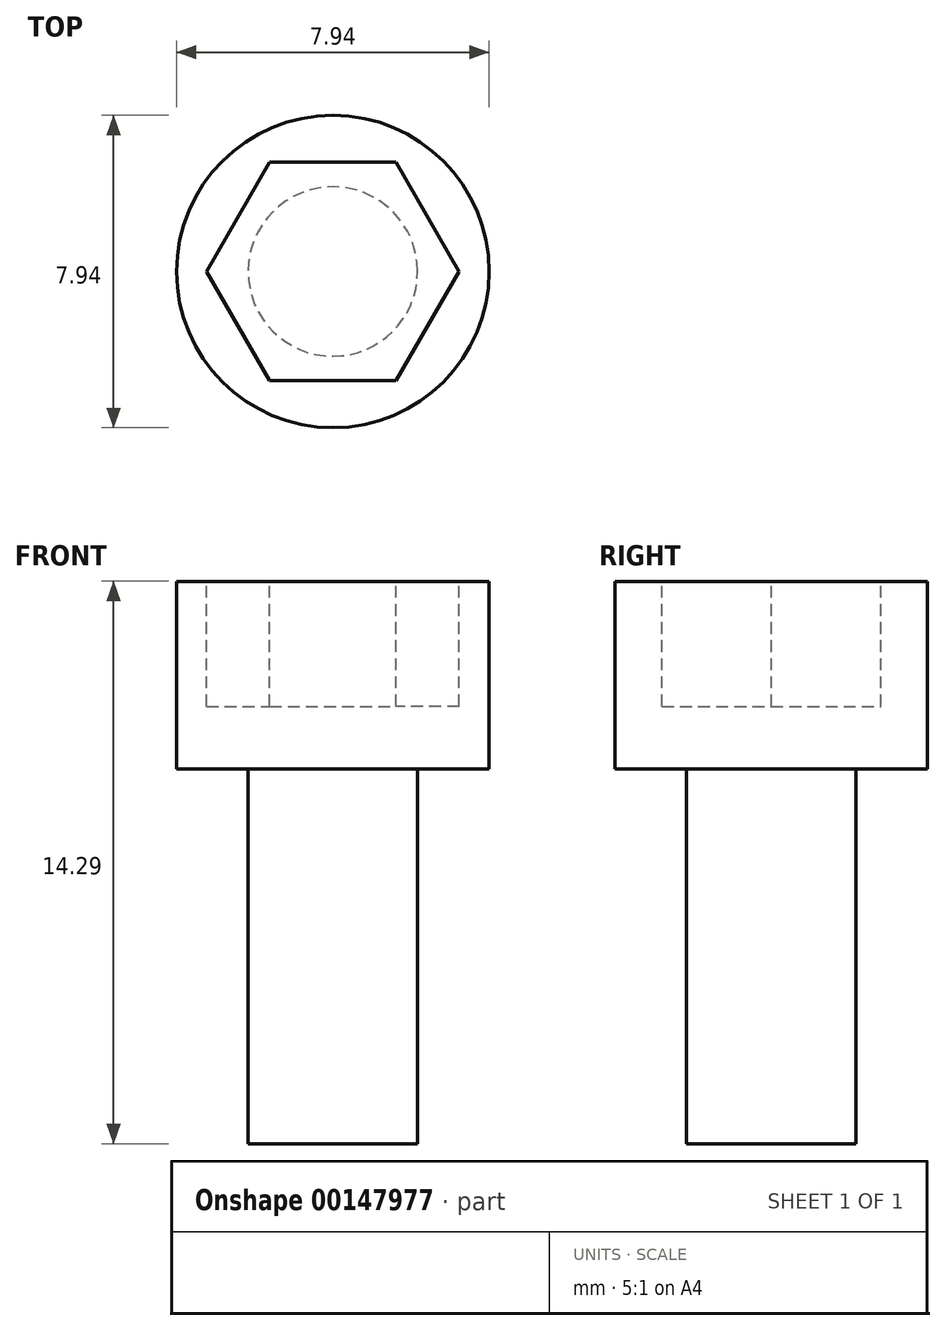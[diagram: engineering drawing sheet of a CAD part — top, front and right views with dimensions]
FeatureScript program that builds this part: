
annotation { "Feature Type Name" : "Feature", "Feature Type Description" : "" }
export const myFeature = defineFeature(function(context is Context, id is Id, definition is map)
    precondition{}
    {
        {
            var Q0;
            Q0=qCreatedBy(makeId("Top.planeOp"),FACE);
            var sketch = newSketch(context, id + "F0", { "sketchPlane" : qUnion([Q0])});
            skCircle(sketch, "E0", {"center": v(0, 0) * mm, "radius": 2.15 * mm});
            skSolve(sketch);
        }
        {
            var Q0;
            Q0=qSketchRegion(id+"F0",true);
            extrude(context, id + "F1", {"entities" : qUnion([Q0]), "depth" : 9.52 * mm});
        }
        {
            var Q0;
            Q0=makeQuery(id+"F1.opExtrude","CAP_FACE",FACE,{"disambiguationData":[OSD([sQuery(id+"F0.wireOp",EDGE,"E0")])],"isStart":false});
            var sketch = newSketch(context, id + "F2", { "sketchPlane" : qUnion([Q0])});
            skCircle(sketch, "E1", {"center": v(0, 0) * mm, "radius": 3.97 * mm});
            skSolve(sketch);
        }
        {
            var Q0;
            Q0=qSketchRegion(id+"F2",true);
            extrude(context, id + "F3", {"entities" : qUnion([Q0]), "operationType" : NewBodyOperationType.ADD, "depth" : 4.76 * mm});
        }
        {
            var Q0;
            Q0=makeQuery(id+"F3.opExtrude","CAP_FACE",FACE,{"disambiguationData":[OSD([sQuery(id+"F2.wireOp",EDGE,"E1")])],"isStart":false});
            var sketch = newSketch(context, id + "F4", { "sketchPlane" : qUnion([Q0])});
            skCircle(sketch, "E2.cCircle", {"center": v(0, 0) * mm, "radius": 2.78 * mm, "construction": true});
            skLineSegment(sketch, "E2.0", {"start": v(-1.6, 2.78) * mm, "end": v(1.6, 2.78) * mm});
            skLineSegment(sketch, "E2.1", {"start": v(1.6, 2.78) * mm, "end": v(3.2, 0) * mm});
            skLineSegment(sketch, "E2.2", {"start": v(3.2, 0) * mm, "end": v(1.6, -2.78) * mm});
            skLineSegment(sketch, "E2.3", {"start": v(1.6, -2.78) * mm, "end": v(-1.6, -2.78) * mm});
            skLineSegment(sketch, "E2.4", {"start": v(-1.6, -2.78) * mm, "end": v(-3.2, 0) * mm});
            skLineSegment(sketch, "E2.5", {"start": v(-3.2, 0) * mm, "end": v(-1.6, 2.78) * mm});
            skPoint(sketch, "E2.0.midPoint", {"position": v(0, 2.78) * mm});
            skSolve(sketch);
        }
        {
            var Q0;
            Q0=qSketchRegion(id+"F4",true);
            extrude(context, id + "F5", {"entities" : qUnion([Q0]), "operationType" : NewBodyOperationType.REMOVE, "oppositeDirection" : true, "depth" : 3.17 * mm});
        }
    });
